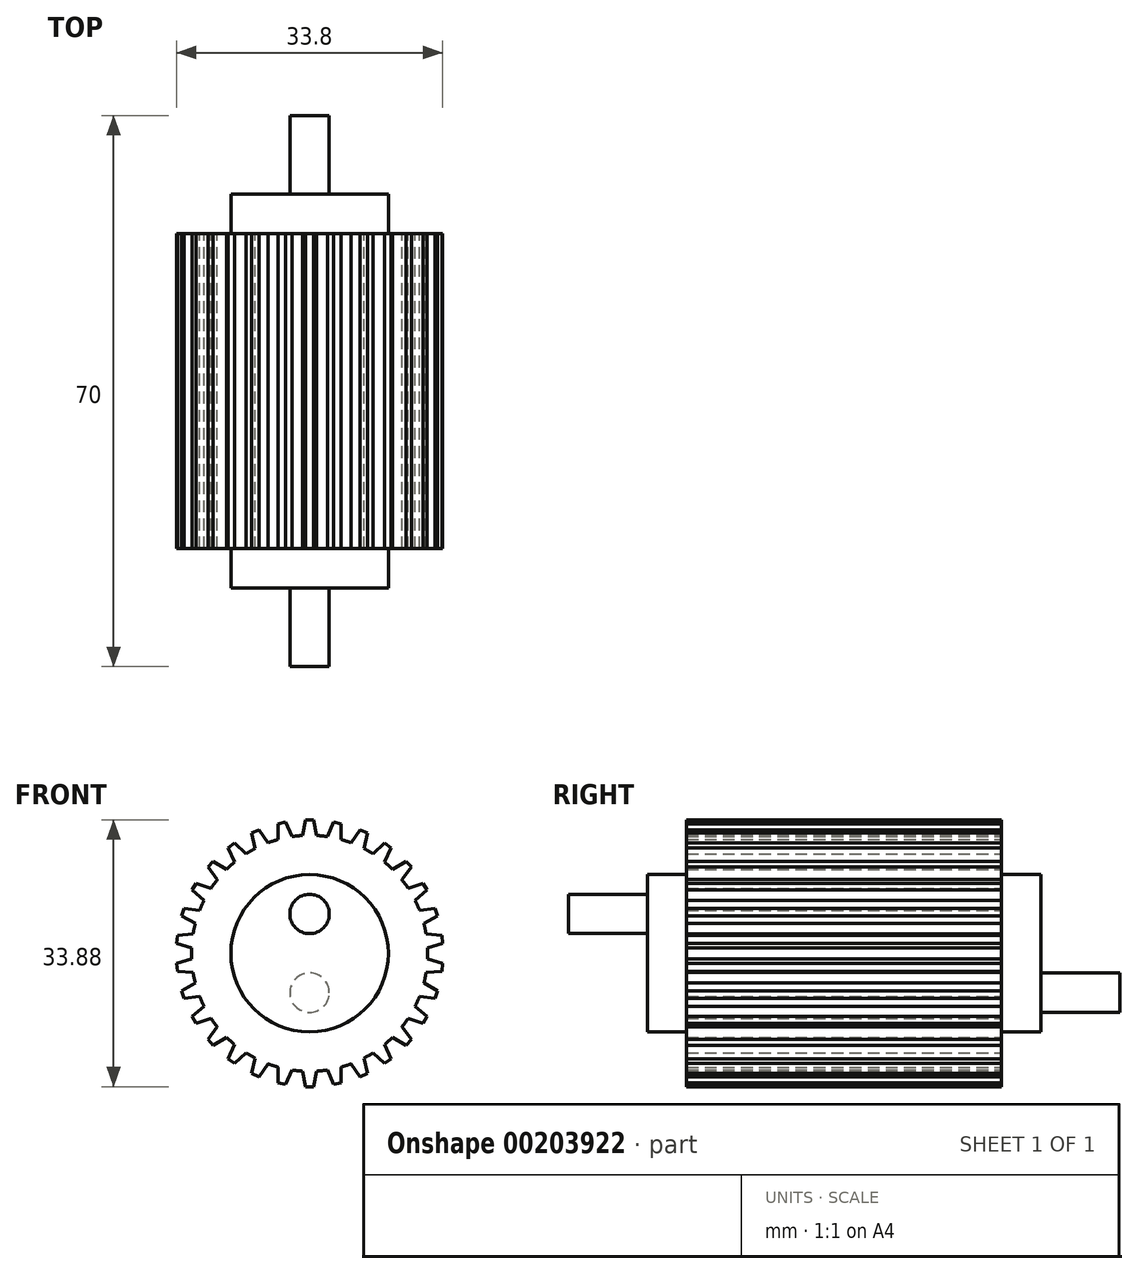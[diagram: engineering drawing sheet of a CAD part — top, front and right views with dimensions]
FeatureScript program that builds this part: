
annotation { "Feature Type Name" : "Feature", "Feature Type Description" : "" }
export const myFeature = defineFeature(function(context is Context, id is Id, definition is map)
    precondition{}
    {
        {
            var Q0;
            Q0=qCreatedBy(makeId("Front.planeOp"),FACE);
            var sketch = newSketch(context, id + "F0", { "sketchPlane" : qUnion([Q0])});
            skCircle(sketch, "E0", {"center": v(0, 0) * mm, "radius": 15 * mm});
            skLineSegment(sketch, "E1", {"start": v(0, 0) * mm, "end": v(0, 16.94) * mm, "construction": true});
            skLineSegment(sketch, "E2", {"start": v(0, 16.94) * mm, "end": v(-0.5, 16.94) * mm});
            skLineSegment(sketch, "E3", {"start": v(-0.5, 16.94) * mm, "end": v(-0.88, 14.97) * mm});
            skLineSegment(sketch, "E4.MirrorCS", {"start": v(0, 16.94) * mm, "end": v(0.5, 16.94) * mm});
            skLineSegment(sketch, "E5.MirrorCS", {"start": v(0.5, 16.94) * mm, "end": v(0.88, 14.97) * mm});
            skLineSegment(sketch, "E6.1.0", {"start": v(-4.01, 16.46) * mm, "end": v(-3.98, 14.46) * mm});
            skLineSegment(sketch, "E6.1.1", {"start": v(-3.52, 16.57) * mm, "end": v(-4.01, 16.46) * mm});
            skLineSegment(sketch, "E6.1.2", {"start": v(-3.52, 16.57) * mm, "end": v(-3.03, 16.67) * mm});
            skLineSegment(sketch, "E6.1.3", {"start": v(-3.03, 16.67) * mm, "end": v(-2.25, 14.83) * mm});
            skLineSegment(sketch, "E6.2.0", {"start": v(-7.35, 15.27) * mm, "end": v(-6.9, 13.32) * mm});
            skLineSegment(sketch, "E6.2.1", {"start": v(-6.89, 15.47) * mm, "end": v(-7.35, 15.27) * mm});
            skLineSegment(sketch, "E6.2.2", {"start": v(-6.89, 15.47) * mm, "end": v(-6.43, 15.68) * mm});
            skLineSegment(sketch, "E6.2.3", {"start": v(-6.43, 15.68) * mm, "end": v(-5.28, 14.04) * mm});
            skLineSegment(sketch, "E7.2.3.0", {"start": v(-10.36, 13.4) * mm, "end": v(-9.52, 11.6) * mm});
            skLineSegment(sketch, "E7.3.3.0", {"start": v(-9.96, 13.7) * mm, "end": v(-10.36, 13.4) * mm});
            skLineSegment(sketch, "E7.6.3.0", {"start": v(-9.96, 13.7) * mm, "end": v(-9.55, 14) * mm});
            skLineSegment(sketch, "E7.9.3.0", {"start": v(-9.55, 14) * mm, "end": v(-8.09, 12.63) * mm});
            skLineSegment(sketch, "E7.2.4.0", {"start": v(-12.92, 10.96) * mm, "end": v(-11.72, 9.36) * mm});
            skLineSegment(sketch, "E7.3.4.0", {"start": v(-12.59, 11.33) * mm, "end": v(-12.92, 10.96) * mm});
            skLineSegment(sketch, "E7.6.4.0", {"start": v(-12.59, 11.33) * mm, "end": v(-12.25, 11.7) * mm});
            skLineSegment(sketch, "E7.9.4.0", {"start": v(-12.25, 11.7) * mm, "end": v(-10.54, 10.68) * mm});
            skLineSegment(sketch, "E7.2.5.0", {"start": v(-14.92, 8.04) * mm, "end": v(-13.4, 6.72) * mm});
            skLineSegment(sketch, "E7.3.5.0", {"start": v(-14.67, 8.47) * mm, "end": v(-14.92, 8.04) * mm});
            skLineSegment(sketch, "E7.6.5.0", {"start": v(-14.67, 8.47) * mm, "end": v(-14.42, 8.9) * mm});
            skLineSegment(sketch, "E7.9.5.0", {"start": v(-14.42, 8.9) * mm, "end": v(-12.53, 8.25) * mm});
            skLineSegment(sketch, "E7.2.6.0", {"start": v(-16.26, 4.76) * mm, "end": v(-14.51, 3.79) * mm});
            skLineSegment(sketch, "E7.3.6.0", {"start": v(-16.1, 5.23) * mm, "end": v(-16.26, 4.76) * mm});
            skLineSegment(sketch, "E7.6.6.0", {"start": v(-16.1, 5.23) * mm, "end": v(-15.95, 5.7) * mm});
            skLineSegment(sketch, "E7.9.6.0", {"start": v(-15.95, 5.7) * mm, "end": v(-13.97, 5.47) * mm});
            skLineSegment(sketch, "E7.2.7.0", {"start": v(-16.9, 1.27) * mm, "end": v(-14.98, 0.69) * mm});
            skLineSegment(sketch, "E7.3.7.0", {"start": v(-16.84, 1.77) * mm, "end": v(-16.9, 1.27) * mm});
            skLineSegment(sketch, "E7.6.7.0", {"start": v(-16.84, 1.77) * mm, "end": v(-16.8, 2.27) * mm});
            skLineSegment(sketch, "E7.9.7.0", {"start": v(-16.8, 2.27) * mm, "end": v(-14.8, 2.44) * mm});
            skLineSegment(sketch, "E7.2.8.0", {"start": v(-16.8, -2.27) * mm, "end": v(-14.8, -2.44) * mm});
            skLineSegment(sketch, "E7.3.8.0", {"start": v(-16.84, -1.77) * mm, "end": v(-16.8, -2.27) * mm});
            skLineSegment(sketch, "E7.6.8.0", {"start": v(-16.84, -1.77) * mm, "end": v(-16.9, -1.27) * mm});
            skLineSegment(sketch, "E7.9.8.0", {"start": v(-16.9, -1.27) * mm, "end": v(-14.98, -0.69) * mm});
            skLineSegment(sketch, "E7.2.9.0", {"start": v(-15.95, -5.7) * mm, "end": v(-13.97, -5.47) * mm});
            skLineSegment(sketch, "E7.3.9.0", {"start": v(-16.1, -5.23) * mm, "end": v(-15.95, -5.7) * mm});
            skLineSegment(sketch, "E7.6.9.0", {"start": v(-16.1, -5.23) * mm, "end": v(-16.26, -4.76) * mm});
            skLineSegment(sketch, "E7.9.9.0", {"start": v(-16.26, -4.76) * mm, "end": v(-14.51, -3.79) * mm});
            skLineSegment(sketch, "E7.2.10.0", {"start": v(-14.42, -8.9) * mm, "end": v(-12.53, -8.25) * mm});
            skLineSegment(sketch, "E7.3.10.0", {"start": v(-14.67, -8.47) * mm, "end": v(-14.42, -8.9) * mm});
            skLineSegment(sketch, "E7.6.10.0", {"start": v(-14.67, -8.47) * mm, "end": v(-14.92, -8.04) * mm});
            skLineSegment(sketch, "E7.9.10.0", {"start": v(-14.92, -8.04) * mm, "end": v(-13.4, -6.72) * mm});
            skLineSegment(sketch, "E7.2.11.0", {"start": v(-12.25, -11.7) * mm, "end": v(-10.54, -10.68) * mm});
            skLineSegment(sketch, "E7.3.11.0", {"start": v(-12.59, -11.33) * mm, "end": v(-12.25, -11.7) * mm});
            skLineSegment(sketch, "E7.6.11.0", {"start": v(-12.59, -11.33) * mm, "end": v(-12.92, -10.96) * mm});
            skLineSegment(sketch, "E7.9.11.0", {"start": v(-12.92, -10.96) * mm, "end": v(-11.72, -9.36) * mm});
            skLineSegment(sketch, "E7.2.12.0", {"start": v(-9.55, -14) * mm, "end": v(-8.09, -12.63) * mm});
            skLineSegment(sketch, "E7.3.12.0", {"start": v(-9.96, -13.7) * mm, "end": v(-9.55, -14) * mm});
            skLineSegment(sketch, "E7.6.12.0", {"start": v(-9.96, -13.7) * mm, "end": v(-10.36, -13.4) * mm});
            skLineSegment(sketch, "E7.9.12.0", {"start": v(-10.36, -13.4) * mm, "end": v(-9.52, -11.6) * mm});
            skLineSegment(sketch, "E7.2.13.0", {"start": v(-6.43, -15.68) * mm, "end": v(-5.28, -14.04) * mm});
            skLineSegment(sketch, "E7.3.13.0", {"start": v(-6.89, -15.47) * mm, "end": v(-6.43, -15.68) * mm});
            skLineSegment(sketch, "E7.6.13.0", {"start": v(-6.89, -15.47) * mm, "end": v(-7.35, -15.27) * mm});
            skLineSegment(sketch, "E7.9.13.0", {"start": v(-7.35, -15.27) * mm, "end": v(-6.9, -13.32) * mm});
            skLineSegment(sketch, "E7.2.14.0", {"start": v(-3.03, -16.67) * mm, "end": v(-2.25, -14.83) * mm});
            skLineSegment(sketch, "E7.3.14.0", {"start": v(-3.52, -16.57) * mm, "end": v(-3.03, -16.67) * mm});
            skLineSegment(sketch, "E7.6.14.0", {"start": v(-3.52, -16.57) * mm, "end": v(-4.01, -16.46) * mm});
            skLineSegment(sketch, "E7.9.14.0", {"start": v(-4.01, -16.46) * mm, "end": v(-3.98, -14.46) * mm});
            skLineSegment(sketch, "E8.2.15.0", {"start": v(0.5, -16.94) * mm, "end": v(0.88, -14.97) * mm});
            skLineSegment(sketch, "E8.3.15.0", {"start": v(0, -16.94) * mm, "end": v(0.5, -16.94) * mm});
            skLineSegment(sketch, "E8.6.15.0", {"start": v(0, -16.94) * mm, "end": v(-0.5, -16.94) * mm});
            skLineSegment(sketch, "E8.9.15.0", {"start": v(-0.5, -16.94) * mm, "end": v(-0.88, -14.97) * mm});
            skLineSegment(sketch, "E8.2.16.0", {"start": v(4.01, -16.46) * mm, "end": v(3.98, -14.46) * mm});
            skLineSegment(sketch, "E8.3.16.0", {"start": v(3.52, -16.57) * mm, "end": v(4.01, -16.46) * mm});
            skLineSegment(sketch, "E8.6.16.0", {"start": v(3.52, -16.57) * mm, "end": v(3.03, -16.67) * mm});
            skLineSegment(sketch, "E8.9.16.0", {"start": v(3.03, -16.67) * mm, "end": v(2.25, -14.83) * mm});
            skLineSegment(sketch, "E8.2.17.0", {"start": v(7.35, -15.27) * mm, "end": v(6.9, -13.32) * mm});
            skLineSegment(sketch, "E8.3.17.0", {"start": v(6.89, -15.47) * mm, "end": v(7.35, -15.27) * mm});
            skLineSegment(sketch, "E8.6.17.0", {"start": v(6.89, -15.47) * mm, "end": v(6.43, -15.68) * mm});
            skLineSegment(sketch, "E8.9.17.0", {"start": v(6.43, -15.68) * mm, "end": v(5.28, -14.04) * mm});
            skLineSegment(sketch, "E8.2.18.0", {"start": v(10.36, -13.4) * mm, "end": v(9.52, -11.6) * mm});
            skLineSegment(sketch, "E8.3.18.0", {"start": v(9.96, -13.7) * mm, "end": v(10.36, -13.4) * mm});
            skLineSegment(sketch, "E8.6.18.0", {"start": v(9.96, -13.7) * mm, "end": v(9.55, -14) * mm});
            skLineSegment(sketch, "E8.9.18.0", {"start": v(9.55, -14) * mm, "end": v(8.09, -12.63) * mm});
            skLineSegment(sketch, "E8.2.19.0", {"start": v(12.92, -10.96) * mm, "end": v(11.72, -9.36) * mm});
            skLineSegment(sketch, "E8.3.19.0", {"start": v(12.59, -11.33) * mm, "end": v(12.92, -10.96) * mm});
            skLineSegment(sketch, "E8.6.19.0", {"start": v(12.59, -11.33) * mm, "end": v(12.25, -11.7) * mm});
            skLineSegment(sketch, "E8.9.19.0", {"start": v(12.25, -11.7) * mm, "end": v(10.54, -10.68) * mm});
            skLineSegment(sketch, "E8.2.20.0", {"start": v(14.92, -8.04) * mm, "end": v(13.4, -6.72) * mm});
            skLineSegment(sketch, "E8.3.20.0", {"start": v(14.67, -8.47) * mm, "end": v(14.92, -8.04) * mm});
            skLineSegment(sketch, "E8.6.20.0", {"start": v(14.67, -8.47) * mm, "end": v(14.42, -8.9) * mm});
            skLineSegment(sketch, "E8.9.20.0", {"start": v(14.42, -8.9) * mm, "end": v(12.53, -8.25) * mm});
            skLineSegment(sketch, "E8.2.21.0", {"start": v(16.26, -4.76) * mm, "end": v(14.51, -3.79) * mm});
            skLineSegment(sketch, "E8.3.21.0", {"start": v(16.1, -5.23) * mm, "end": v(16.26, -4.76) * mm});
            skLineSegment(sketch, "E8.6.21.0", {"start": v(16.1, -5.23) * mm, "end": v(15.95, -5.7) * mm});
            skLineSegment(sketch, "E8.9.21.0", {"start": v(15.95, -5.7) * mm, "end": v(13.97, -5.47) * mm});
            skLineSegment(sketch, "E8.2.22.0", {"start": v(16.9, -1.27) * mm, "end": v(14.98, -0.69) * mm});
            skLineSegment(sketch, "E8.3.22.0", {"start": v(16.84, -1.77) * mm, "end": v(16.9, -1.27) * mm});
            skLineSegment(sketch, "E8.6.22.0", {"start": v(16.84, -1.77) * mm, "end": v(16.8, -2.27) * mm});
            skLineSegment(sketch, "E8.9.22.0", {"start": v(16.8, -2.27) * mm, "end": v(14.8, -2.44) * mm});
            skLineSegment(sketch, "E8.2.23.0", {"start": v(16.8, 2.27) * mm, "end": v(14.8, 2.44) * mm});
            skLineSegment(sketch, "E8.3.23.0", {"start": v(16.84, 1.77) * mm, "end": v(16.8, 2.27) * mm});
            skLineSegment(sketch, "E8.6.23.0", {"start": v(16.84, 1.77) * mm, "end": v(16.9, 1.27) * mm});
            skLineSegment(sketch, "E8.9.23.0", {"start": v(16.9, 1.27) * mm, "end": v(14.98, 0.69) * mm});
            skLineSegment(sketch, "E8.2.24.0", {"start": v(15.95, 5.7) * mm, "end": v(13.97, 5.47) * mm});
            skLineSegment(sketch, "E8.3.24.0", {"start": v(16.1, 5.23) * mm, "end": v(15.95, 5.7) * mm});
            skLineSegment(sketch, "E8.6.24.0", {"start": v(16.1, 5.23) * mm, "end": v(16.26, 4.76) * mm});
            skLineSegment(sketch, "E8.9.24.0", {"start": v(16.26, 4.76) * mm, "end": v(14.51, 3.79) * mm});
            skLineSegment(sketch, "E9.2.25.0", {"start": v(14.42, 8.9) * mm, "end": v(12.53, 8.25) * mm});
            skLineSegment(sketch, "E9.3.25.0", {"start": v(14.67, 8.47) * mm, "end": v(14.42, 8.9) * mm});
            skLineSegment(sketch, "E9.6.25.0", {"start": v(14.67, 8.47) * mm, "end": v(14.92, 8.04) * mm});
            skLineSegment(sketch, "E9.9.25.0", {"start": v(14.92, 8.04) * mm, "end": v(13.4, 6.72) * mm});
            skLineSegment(sketch, "E9.2.26.0", {"start": v(12.25, 11.7) * mm, "end": v(10.54, 10.68) * mm});
            skLineSegment(sketch, "E9.3.26.0", {"start": v(12.59, 11.33) * mm, "end": v(12.25, 11.7) * mm});
            skLineSegment(sketch, "E9.6.26.0", {"start": v(12.59, 11.33) * mm, "end": v(12.92, 10.96) * mm});
            skLineSegment(sketch, "E9.9.26.0", {"start": v(12.92, 10.96) * mm, "end": v(11.72, 9.36) * mm});
            skLineSegment(sketch, "E9.2.27.0", {"start": v(9.55, 14) * mm, "end": v(8.09, 12.63) * mm});
            skLineSegment(sketch, "E9.3.27.0", {"start": v(9.96, 13.7) * mm, "end": v(9.55, 14) * mm});
            skLineSegment(sketch, "E9.6.27.0", {"start": v(9.96, 13.7) * mm, "end": v(10.36, 13.4) * mm});
            skLineSegment(sketch, "E9.9.27.0", {"start": v(10.36, 13.4) * mm, "end": v(9.52, 11.6) * mm});
            skLineSegment(sketch, "E9.2.28.0", {"start": v(6.43, 15.68) * mm, "end": v(5.28, 14.04) * mm});
            skLineSegment(sketch, "E9.3.28.0", {"start": v(6.89, 15.47) * mm, "end": v(6.43, 15.68) * mm});
            skLineSegment(sketch, "E9.6.28.0", {"start": v(6.89, 15.47) * mm, "end": v(7.35, 15.27) * mm});
            skLineSegment(sketch, "E9.9.28.0", {"start": v(7.35, 15.27) * mm, "end": v(6.9, 13.32) * mm});
            skLineSegment(sketch, "E9.2.29.0", {"start": v(3.03, 16.67) * mm, "end": v(2.25, 14.83) * mm});
            skLineSegment(sketch, "E9.3.29.0", {"start": v(3.52, 16.57) * mm, "end": v(3.03, 16.67) * mm});
            skLineSegment(sketch, "E9.6.29.0", {"start": v(3.52, 16.57) * mm, "end": v(4.01, 16.46) * mm});
            skLineSegment(sketch, "E9.9.29.0", {"start": v(4.01, 16.46) * mm, "end": v(3.98, 14.46) * mm});
            skSolve(sketch);
        }
        {
            var Q0;
            Q0=qSketchRegion(id+"F0",true);
            extrude(context, id + "F1", {"entities" : qUnion([Q0]), "depth" : 40 * mm});
        }
        {
            var Q0;
            Q0=makeQuery(id+"F1.opExtrude","CAP_FACE",FACE,{"disambiguationData":[OSD([sQuery(id+"F0.wireOp",EDGE,"E0"),sQuery(id+"F0.wireOp",EDGE,"E2"),sQuery(id+"F0.wireOp",EDGE,"E3"),sQuery(id+"F0.wireOp",EDGE,"E4.MirrorCS"),sQuery(id+"F0.wireOp",EDGE,"E5.MirrorCS"),sQuery(id+"F0.wireOp",EDGE,"E6.1.0"),sQuery(id+"F0.wireOp",EDGE,"E6.1.1"),sQuery(id+"F0.wireOp",EDGE,"E6.1.2"),sQuery(id+"F0.wireOp",EDGE,"E6.1.3"),sQuery(id+"F0.wireOp",EDGE,"E6.2.0"),sQuery(id+"F0.wireOp",EDGE,"E6.2.1"),sQuery(id+"F0.wireOp",EDGE,"E6.2.2"),sQuery(id+"F0.wireOp",EDGE,"E6.2.3"),sQuery(id+"F0.wireOp",EDGE,"E7.2.3.0"),sQuery(id+"F0.wireOp",EDGE,"E7.3.3.0"),sQuery(id+"F0.wireOp",EDGE,"E7.6.3.0"),sQuery(id+"F0.wireOp",EDGE,"E7.9.3.0"),sQuery(id+"F0.wireOp",EDGE,"E7.2.4.0"),sQuery(id+"F0.wireOp",EDGE,"E7.3.4.0"),sQuery(id+"F0.wireOp",EDGE,"E7.6.4.0"),sQuery(id+"F0.wireOp",EDGE,"E7.9.4.0"),sQuery(id+"F0.wireOp",EDGE,"E7.2.5.0"),sQuery(id+"F0.wireOp",EDGE,"E7.3.5.0"),sQuery(id+"F0.wireOp",EDGE,"E7.6.5.0"),sQuery(id+"F0.wireOp",EDGE,"E7.9.5.0"),sQuery(id+"F0.wireOp",EDGE,"E7.2.6.0"),sQuery(id+"F0.wireOp",EDGE,"E7.3.6.0"),sQuery(id+"F0.wireOp",EDGE,"E7.6.6.0"),sQuery(id+"F0.wireOp",EDGE,"E7.9.6.0"),sQuery(id+"F0.wireOp",EDGE,"E7.2.7.0"),sQuery(id+"F0.wireOp",EDGE,"E7.3.7.0"),sQuery(id+"F0.wireOp",EDGE,"E7.6.7.0"),sQuery(id+"F0.wireOp",EDGE,"E7.9.7.0"),sQuery(id+"F0.wireOp",EDGE,"E7.2.8.0"),sQuery(id+"F0.wireOp",EDGE,"E7.3.8.0"),sQuery(id+"F0.wireOp",EDGE,"E7.6.8.0"),sQuery(id+"F0.wireOp",EDGE,"E7.9.8.0"),sQuery(id+"F0.wireOp",EDGE,"E7.2.9.0"),sQuery(id+"F0.wireOp",EDGE,"E7.3.9.0"),sQuery(id+"F0.wireOp",EDGE,"E7.6.9.0"),sQuery(id+"F0.wireOp",EDGE,"E7.9.9.0"),sQuery(id+"F0.wireOp",EDGE,"E7.2.10.0"),sQuery(id+"F0.wireOp",EDGE,"E7.3.10.0"),sQuery(id+"F0.wireOp",EDGE,"E7.6.10.0"),sQuery(id+"F0.wireOp",EDGE,"E7.9.10.0"),sQuery(id+"F0.wireOp",EDGE,"E7.2.11.0"),sQuery(id+"F0.wireOp",EDGE,"E7.3.11.0"),sQuery(id+"F0.wireOp",EDGE,"E7.6.11.0"),sQuery(id+"F0.wireOp",EDGE,"E7.9.11.0"),sQuery(id+"F0.wireOp",EDGE,"E7.2.12.0"),sQuery(id+"F0.wireOp",EDGE,"E7.3.12.0"),sQuery(id+"F0.wireOp",EDGE,"E7.6.12.0"),sQuery(id+"F0.wireOp",EDGE,"E7.9.12.0"),sQuery(id+"F0.wireOp",EDGE,"E7.2.13.0"),sQuery(id+"F0.wireOp",EDGE,"E7.3.13.0"),sQuery(id+"F0.wireOp",EDGE,"E7.6.13.0"),sQuery(id+"F0.wireOp",EDGE,"E7.9.13.0"),sQuery(id+"F0.wireOp",EDGE,"E7.2.14.0"),sQuery(id+"F0.wireOp",EDGE,"E7.3.14.0"),sQuery(id+"F0.wireOp",EDGE,"E7.6.14.0"),sQuery(id+"F0.wireOp",EDGE,"E7.9.14.0"),sQuery(id+"F0.wireOp",EDGE,"E8.2.15.0"),sQuery(id+"F0.wireOp",EDGE,"E8.3.15.0"),sQuery(id+"F0.wireOp",EDGE,"E8.6.15.0"),sQuery(id+"F0.wireOp",EDGE,"E8.9.15.0"),sQuery(id+"F0.wireOp",EDGE,"E8.2.16.0"),sQuery(id+"F0.wireOp",EDGE,"E8.3.16.0"),sQuery(id+"F0.wireOp",EDGE,"E8.6.16.0"),sQuery(id+"F0.wireOp",EDGE,"E8.9.16.0"),sQuery(id+"F0.wireOp",EDGE,"E8.2.17.0"),sQuery(id+"F0.wireOp",EDGE,"E8.3.17.0"),sQuery(id+"F0.wireOp",EDGE,"E8.6.17.0"),sQuery(id+"F0.wireOp",EDGE,"E8.9.17.0"),sQuery(id+"F0.wireOp",EDGE,"E8.2.18.0"),sQuery(id+"F0.wireOp",EDGE,"E8.3.18.0"),sQuery(id+"F0.wireOp",EDGE,"E8.6.18.0"),sQuery(id+"F0.wireOp",EDGE,"E8.9.18.0"),sQuery(id+"F0.wireOp",EDGE,"E8.2.19.0"),sQuery(id+"F0.wireOp",EDGE,"E8.3.19.0"),sQuery(id+"F0.wireOp",EDGE,"E8.6.19.0"),sQuery(id+"F0.wireOp",EDGE,"E8.9.19.0"),sQuery(id+"F0.wireOp",EDGE,"E8.2.20.0"),sQuery(id+"F0.wireOp",EDGE,"E8.3.20.0"),sQuery(id+"F0.wireOp",EDGE,"E8.6.20.0"),sQuery(id+"F0.wireOp",EDGE,"E8.9.20.0"),sQuery(id+"F0.wireOp",EDGE,"E8.2.21.0"),sQuery(id+"F0.wireOp",EDGE,"E8.3.21.0"),sQuery(id+"F0.wireOp",EDGE,"E8.6.21.0"),sQuery(id+"F0.wireOp",EDGE,"E8.9.21.0"),sQuery(id+"F0.wireOp",EDGE,"E8.2.22.0"),sQuery(id+"F0.wireOp",EDGE,"E8.3.22.0"),sQuery(id+"F0.wireOp",EDGE,"E8.6.22.0"),sQuery(id+"F0.wireOp",EDGE,"E8.9.22.0"),sQuery(id+"F0.wireOp",EDGE,"E8.2.23.0"),sQuery(id+"F0.wireOp",EDGE,"E8.3.23.0"),sQuery(id+"F0.wireOp",EDGE,"E8.6.23.0"),sQuery(id+"F0.wireOp",EDGE,"E8.9.23.0"),sQuery(id+"F0.wireOp",EDGE,"E8.2.24.0"),sQuery(id+"F0.wireOp",EDGE,"E8.3.24.0"),sQuery(id+"F0.wireOp",EDGE,"E8.6.24.0"),sQuery(id+"F0.wireOp",EDGE,"E8.9.24.0"),sQuery(id+"F0.wireOp",EDGE,"E9.2.25.0"),sQuery(id+"F0.wireOp",EDGE,"E9.3.25.0"),sQuery(id+"F0.wireOp",EDGE,"E9.6.25.0"),sQuery(id+"F0.wireOp",EDGE,"E9.9.25.0"),sQuery(id+"F0.wireOp",EDGE,"E9.2.26.0"),sQuery(id+"F0.wireOp",EDGE,"E9.3.26.0"),sQuery(id+"F0.wireOp",EDGE,"E9.6.26.0"),sQuery(id+"F0.wireOp",EDGE,"E9.9.26.0"),sQuery(id+"F0.wireOp",EDGE,"E9.2.27.0"),sQuery(id+"F0.wireOp",EDGE,"E9.3.27.0"),sQuery(id+"F0.wireOp",EDGE,"E9.6.27.0"),sQuery(id+"F0.wireOp",EDGE,"E9.9.27.0"),sQuery(id+"F0.wireOp",EDGE,"E9.2.28.0"),sQuery(id+"F0.wireOp",EDGE,"E9.3.28.0"),sQuery(id+"F0.wireOp",EDGE,"E9.6.28.0"),sQuery(id+"F0.wireOp",EDGE,"E9.9.28.0"),sQuery(id+"F0.wireOp",EDGE,"E9.2.29.0"),sQuery(id+"F0.wireOp",EDGE,"E9.3.29.0"),sQuery(id+"F0.wireOp",EDGE,"E9.6.29.0"),sQuery(id+"F0.wireOp",EDGE,"E9.9.29.0")])],"isStart":true});
            var sketch = newSketch(context, id + "F2", { "sketchPlane" : qUnion([Q0])});
            skCircle(sketch, "E10", {"center": v(0, 0) * mm, "radius": 10 * mm});
            skSolve(sketch);
        }
        {
            var Q0;
            Q0=qSketchRegion(id+"F2",true);
            extrude(context, id + "F3", {"entities" : qUnion([Q0]), "operationType" : NewBodyOperationType.ADD, "depth" : 5 * mm});
        }
        {
            var Q0;
            Q0=makeQuery(id+"F1.opExtrude","CAP_FACE",FACE,{"disambiguationData":[OSD([sQuery(id+"F0.wireOp",EDGE,"E0"),sQuery(id+"F0.wireOp",EDGE,"E2"),sQuery(id+"F0.wireOp",EDGE,"E3"),sQuery(id+"F0.wireOp",EDGE,"E4.MirrorCS"),sQuery(id+"F0.wireOp",EDGE,"E5.MirrorCS"),sQuery(id+"F0.wireOp",EDGE,"E6.1.0"),sQuery(id+"F0.wireOp",EDGE,"E6.1.1"),sQuery(id+"F0.wireOp",EDGE,"E6.1.2"),sQuery(id+"F0.wireOp",EDGE,"E6.1.3"),sQuery(id+"F0.wireOp",EDGE,"E6.2.0"),sQuery(id+"F0.wireOp",EDGE,"E6.2.1"),sQuery(id+"F0.wireOp",EDGE,"E6.2.2"),sQuery(id+"F0.wireOp",EDGE,"E6.2.3"),sQuery(id+"F0.wireOp",EDGE,"E7.2.3.0"),sQuery(id+"F0.wireOp",EDGE,"E7.3.3.0"),sQuery(id+"F0.wireOp",EDGE,"E7.6.3.0"),sQuery(id+"F0.wireOp",EDGE,"E7.9.3.0"),sQuery(id+"F0.wireOp",EDGE,"E7.2.4.0"),sQuery(id+"F0.wireOp",EDGE,"E7.3.4.0"),sQuery(id+"F0.wireOp",EDGE,"E7.6.4.0"),sQuery(id+"F0.wireOp",EDGE,"E7.9.4.0"),sQuery(id+"F0.wireOp",EDGE,"E7.2.5.0"),sQuery(id+"F0.wireOp",EDGE,"E7.3.5.0"),sQuery(id+"F0.wireOp",EDGE,"E7.6.5.0"),sQuery(id+"F0.wireOp",EDGE,"E7.9.5.0"),sQuery(id+"F0.wireOp",EDGE,"E7.2.6.0"),sQuery(id+"F0.wireOp",EDGE,"E7.3.6.0"),sQuery(id+"F0.wireOp",EDGE,"E7.6.6.0"),sQuery(id+"F0.wireOp",EDGE,"E7.9.6.0"),sQuery(id+"F0.wireOp",EDGE,"E7.2.7.0"),sQuery(id+"F0.wireOp",EDGE,"E7.3.7.0"),sQuery(id+"F0.wireOp",EDGE,"E7.6.7.0"),sQuery(id+"F0.wireOp",EDGE,"E7.9.7.0"),sQuery(id+"F0.wireOp",EDGE,"E7.2.8.0"),sQuery(id+"F0.wireOp",EDGE,"E7.3.8.0"),sQuery(id+"F0.wireOp",EDGE,"E7.6.8.0"),sQuery(id+"F0.wireOp",EDGE,"E7.9.8.0"),sQuery(id+"F0.wireOp",EDGE,"E7.2.9.0"),sQuery(id+"F0.wireOp",EDGE,"E7.3.9.0"),sQuery(id+"F0.wireOp",EDGE,"E7.6.9.0"),sQuery(id+"F0.wireOp",EDGE,"E7.9.9.0"),sQuery(id+"F0.wireOp",EDGE,"E7.2.10.0"),sQuery(id+"F0.wireOp",EDGE,"E7.3.10.0"),sQuery(id+"F0.wireOp",EDGE,"E7.6.10.0"),sQuery(id+"F0.wireOp",EDGE,"E7.9.10.0"),sQuery(id+"F0.wireOp",EDGE,"E7.2.11.0"),sQuery(id+"F0.wireOp",EDGE,"E7.3.11.0"),sQuery(id+"F0.wireOp",EDGE,"E7.6.11.0"),sQuery(id+"F0.wireOp",EDGE,"E7.9.11.0"),sQuery(id+"F0.wireOp",EDGE,"E7.2.12.0"),sQuery(id+"F0.wireOp",EDGE,"E7.3.12.0"),sQuery(id+"F0.wireOp",EDGE,"E7.6.12.0"),sQuery(id+"F0.wireOp",EDGE,"E7.9.12.0"),sQuery(id+"F0.wireOp",EDGE,"E7.2.13.0"),sQuery(id+"F0.wireOp",EDGE,"E7.3.13.0"),sQuery(id+"F0.wireOp",EDGE,"E7.6.13.0"),sQuery(id+"F0.wireOp",EDGE,"E7.9.13.0"),sQuery(id+"F0.wireOp",EDGE,"E7.2.14.0"),sQuery(id+"F0.wireOp",EDGE,"E7.3.14.0"),sQuery(id+"F0.wireOp",EDGE,"E7.6.14.0"),sQuery(id+"F0.wireOp",EDGE,"E7.9.14.0"),sQuery(id+"F0.wireOp",EDGE,"E8.2.15.0"),sQuery(id+"F0.wireOp",EDGE,"E8.3.15.0"),sQuery(id+"F0.wireOp",EDGE,"E8.6.15.0"),sQuery(id+"F0.wireOp",EDGE,"E8.9.15.0"),sQuery(id+"F0.wireOp",EDGE,"E8.2.16.0"),sQuery(id+"F0.wireOp",EDGE,"E8.3.16.0"),sQuery(id+"F0.wireOp",EDGE,"E8.6.16.0"),sQuery(id+"F0.wireOp",EDGE,"E8.9.16.0"),sQuery(id+"F0.wireOp",EDGE,"E8.2.17.0"),sQuery(id+"F0.wireOp",EDGE,"E8.3.17.0"),sQuery(id+"F0.wireOp",EDGE,"E8.6.17.0"),sQuery(id+"F0.wireOp",EDGE,"E8.9.17.0"),sQuery(id+"F0.wireOp",EDGE,"E8.2.18.0"),sQuery(id+"F0.wireOp",EDGE,"E8.3.18.0"),sQuery(id+"F0.wireOp",EDGE,"E8.6.18.0"),sQuery(id+"F0.wireOp",EDGE,"E8.9.18.0"),sQuery(id+"F0.wireOp",EDGE,"E8.2.19.0"),sQuery(id+"F0.wireOp",EDGE,"E8.3.19.0"),sQuery(id+"F0.wireOp",EDGE,"E8.6.19.0"),sQuery(id+"F0.wireOp",EDGE,"E8.9.19.0"),sQuery(id+"F0.wireOp",EDGE,"E8.2.20.0"),sQuery(id+"F0.wireOp",EDGE,"E8.3.20.0"),sQuery(id+"F0.wireOp",EDGE,"E8.6.20.0"),sQuery(id+"F0.wireOp",EDGE,"E8.9.20.0"),sQuery(id+"F0.wireOp",EDGE,"E8.2.21.0"),sQuery(id+"F0.wireOp",EDGE,"E8.3.21.0"),sQuery(id+"F0.wireOp",EDGE,"E8.6.21.0"),sQuery(id+"F0.wireOp",EDGE,"E8.9.21.0"),sQuery(id+"F0.wireOp",EDGE,"E8.2.22.0"),sQuery(id+"F0.wireOp",EDGE,"E8.3.22.0"),sQuery(id+"F0.wireOp",EDGE,"E8.6.22.0"),sQuery(id+"F0.wireOp",EDGE,"E8.9.22.0"),sQuery(id+"F0.wireOp",EDGE,"E8.2.23.0"),sQuery(id+"F0.wireOp",EDGE,"E8.3.23.0"),sQuery(id+"F0.wireOp",EDGE,"E8.6.23.0"),sQuery(id+"F0.wireOp",EDGE,"E8.9.23.0"),sQuery(id+"F0.wireOp",EDGE,"E8.2.24.0"),sQuery(id+"F0.wireOp",EDGE,"E8.3.24.0"),sQuery(id+"F0.wireOp",EDGE,"E8.6.24.0"),sQuery(id+"F0.wireOp",EDGE,"E8.9.24.0"),sQuery(id+"F0.wireOp",EDGE,"E9.2.25.0"),sQuery(id+"F0.wireOp",EDGE,"E9.3.25.0"),sQuery(id+"F0.wireOp",EDGE,"E9.6.25.0"),sQuery(id+"F0.wireOp",EDGE,"E9.9.25.0"),sQuery(id+"F0.wireOp",EDGE,"E9.2.26.0"),sQuery(id+"F0.wireOp",EDGE,"E9.3.26.0"),sQuery(id+"F0.wireOp",EDGE,"E9.6.26.0"),sQuery(id+"F0.wireOp",EDGE,"E9.9.26.0"),sQuery(id+"F0.wireOp",EDGE,"E9.2.27.0"),sQuery(id+"F0.wireOp",EDGE,"E9.3.27.0"),sQuery(id+"F0.wireOp",EDGE,"E9.6.27.0"),sQuery(id+"F0.wireOp",EDGE,"E9.9.27.0"),sQuery(id+"F0.wireOp",EDGE,"E9.2.28.0"),sQuery(id+"F0.wireOp",EDGE,"E9.3.28.0"),sQuery(id+"F0.wireOp",EDGE,"E9.6.28.0"),sQuery(id+"F0.wireOp",EDGE,"E9.9.28.0"),sQuery(id+"F0.wireOp",EDGE,"E9.2.29.0"),sQuery(id+"F0.wireOp",EDGE,"E9.3.29.0"),sQuery(id+"F0.wireOp",EDGE,"E9.6.29.0"),sQuery(id+"F0.wireOp",EDGE,"E9.9.29.0")])],"isStart":false});
            var sketch = newSketch(context, id + "F4", { "sketchPlane" : qUnion([Q0])});
            skCircle(sketch, "E11", {"center": v(0, 0) * mm, "radius": 10 * mm});
            skSolve(sketch);
        }
        {
            var Q0;
            Q0=qSketchRegion(id+"F4",true);
            extrude(context, id + "F5", {"entities" : qUnion([Q0]), "operationType" : NewBodyOperationType.ADD, "depth" : 5 * mm});
        }
        {
            var Q0;
            Q0=makeQuery(id+"F5.opExtrude","CAP_FACE",FACE,{"disambiguationData":[OSD([sQuery(id+"F4.wireOp",EDGE,"E11")])],"isStart":false});
            var sketch = newSketch(context, id + "F6", { "sketchPlane" : qUnion([Q0])});
            skLineSegment(sketch, "E12", {"start": v(0, 0) * mm, "end": v(0, 10) * mm, "construction": true});
            skCircle(sketch, "E13", {"center": v(0, 5) * mm, "radius": 2.5 * mm});
            skSolve(sketch);
        }
        {
            var Q0;
            Q0=qSketchRegion(id+"F6",true);
            extrude(context, id + "F7", {"entities" : qUnion([Q0]), "operationType" : NewBodyOperationType.ADD, "depth" : 10 * mm});
        }
        {
            var Q0;
            Q0=makeQuery(id+"F3.opExtrude","CAP_FACE",FACE,{"disambiguationData":[OSD([sQuery(id+"F2.wireOp",EDGE,"E10")])],"isStart":false});
            var sketch = newSketch(context, id + "F8", { "sketchPlane" : qUnion([Q0])});
            skLineSegment(sketch, "E14", {"start": v(0, 0) * mm, "end": v(0, -10) * mm, "construction": true});
            skCircle(sketch, "E15", {"center": v(0, -5) * mm, "radius": 2.5 * mm});
            skSolve(sketch);
        }
        {
            var Q0;
            Q0=qSketchRegion(id+"F8",true);
            extrude(context, id + "F9", {"entities" : qUnion([Q0]), "operationType" : NewBodyOperationType.ADD, "depth" : 10 * mm});
        }
    });
